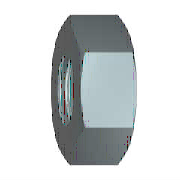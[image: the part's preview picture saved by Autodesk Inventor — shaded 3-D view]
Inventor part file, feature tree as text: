
AUTODESK INVENTOR PART (.ipt)
format: ipt  version: 2016 (Build 200138000, 138)  size: 161,280 bytes
history: native  units: mm (DEFAULTED — no unit token found)
features: sketch x3, chamfer x1, hole x1, other x1, plane x1
ambient origin geometry x7: Origin, YZ Plane, XZ Plane, X Axis, Y Axis, Z Axis, Center Point
bodies: Solid1 (feature_tree), Body (feature_tree)
feature tree (7):
  chamfer  "Chamfer1"  Angle=30.0deg  [1 undecoded]
  hole  "Thread"  [1 undecoded]
  other  "Work Axis1"
  plane  "Work Plane1"
  sketch  "Sketch1"  dims[d0=21.93931mm]
  sketch  "Sketch2"  dims[d1=10.0mm]
  sketch  "Sketch3"  dims[d2=0.0mm d3=30.0deg d4=30.0deg d5=16.5mm d6=16.5mm d7=90.0deg d25=10.106mm d26=6.0mm d27=4.0mm d28=2.0mm d29=14.3117mm d30=8.0mm d31=20.594885mm d8=0.947215mm d9=30.0deg d10=0.947215mm d11=30.0deg d13=0.0mm d14=0.0mm d39=0.0mm d40=0.947215mm d41=0.947215mm d42=0.0mm]
note: 2 required parameter values undecoded (feature->parameter linkage not recoverable at this tier; creation-order binding heuristic only, values carry confidence <= 0.55)
